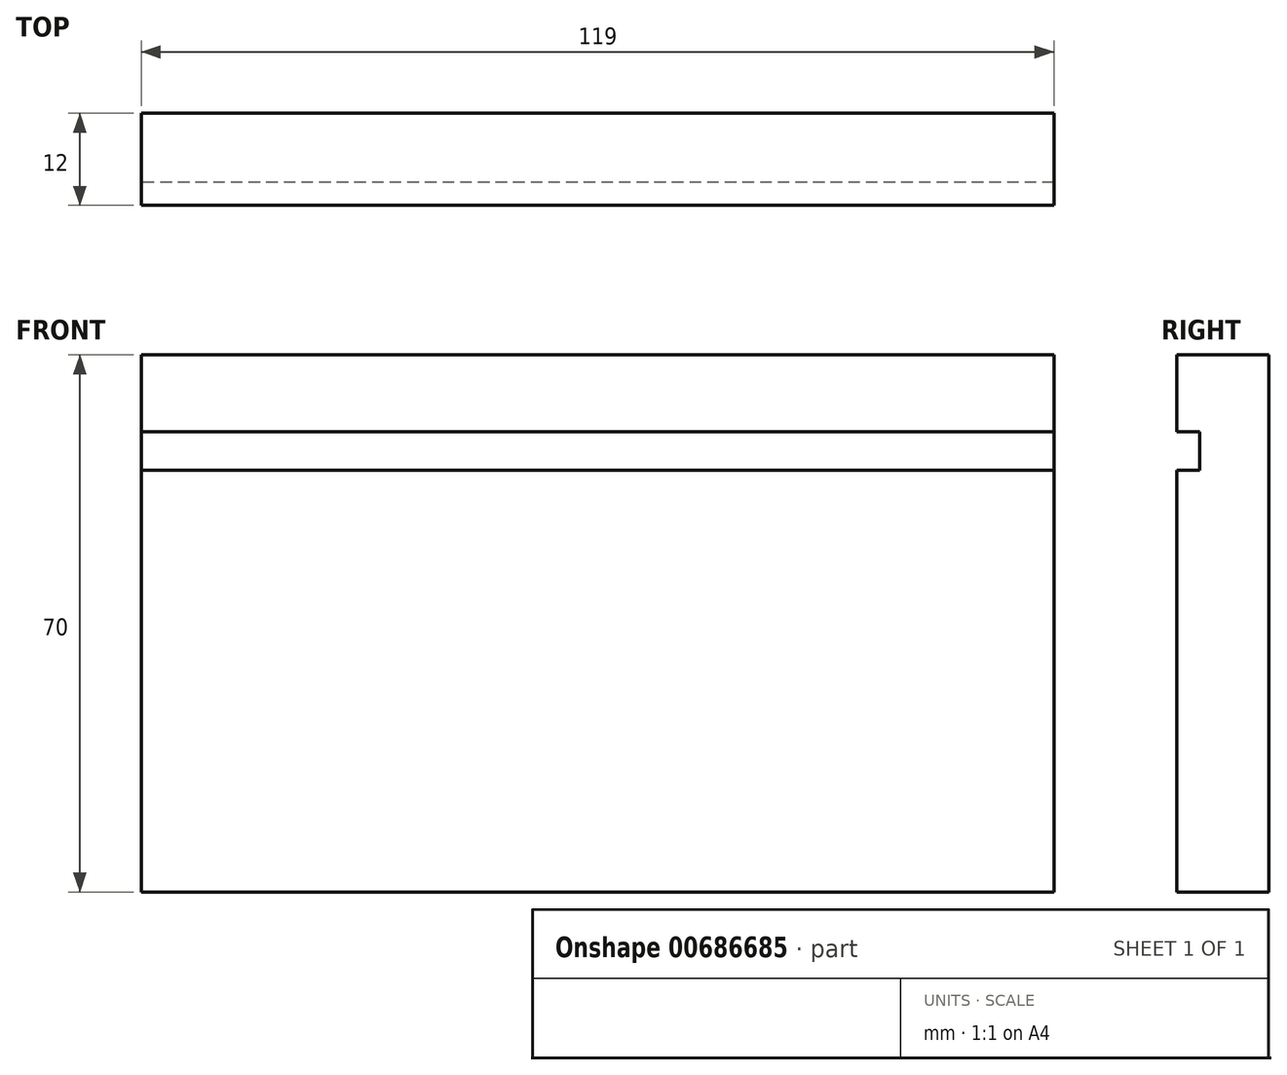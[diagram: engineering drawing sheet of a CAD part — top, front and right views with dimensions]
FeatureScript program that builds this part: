
annotation { "Feature Type Name" : "Feature", "Feature Type Description" : "" }
export const myFeature = defineFeature(function(context is Context, id is Id, definition is map)
    precondition{}
    {
        {
            var Q0;
            Q0=qCreatedBy(makeId("Right.planeOp"),FACE);
            var sketch = newSketch(context, id + "F0", { "sketchPlane" : qUnion([Q0])});
            skLineSegment(sketch, "E0", {"start": v(0, 0) * mm, "end": v(0, 70) * mm});
            skLineSegment(sketch, "E1", {"start": v(0, 70) * mm, "end": v(-12, 70) * mm});
            skLineSegment(sketch, "E2", {"start": v(-12, 70) * mm, "end": v(-12, 60) * mm});
            skLineSegment(sketch, "E3", {"start": v(-9, 60) * mm, "end": v(-12, 60) * mm});
            skLineSegment(sketch, "E4", {"start": v(-9, 60) * mm, "end": v(-9, 55) * mm});
            skLineSegment(sketch, "E5", {"start": v(-9, 55) * mm, "end": v(-12, 55) * mm});
            skLineSegment(sketch, "E6", {"start": v(-12, 55) * mm, "end": v(-12, 0) * mm});
            skLineSegment(sketch, "E7", {"start": v(-12, 0) * mm, "end": v(0, 0) * mm});
            skSolve(sketch);
        }
        {
            var Q0;
            Q0=qSketchRegion(id+"F0",true);
            extrude(context, id + "F1", {"entities" : qUnion([Q0]), "depth" : 119 * mm, "offsetDistance" : 25 * mm});
        }
    });
